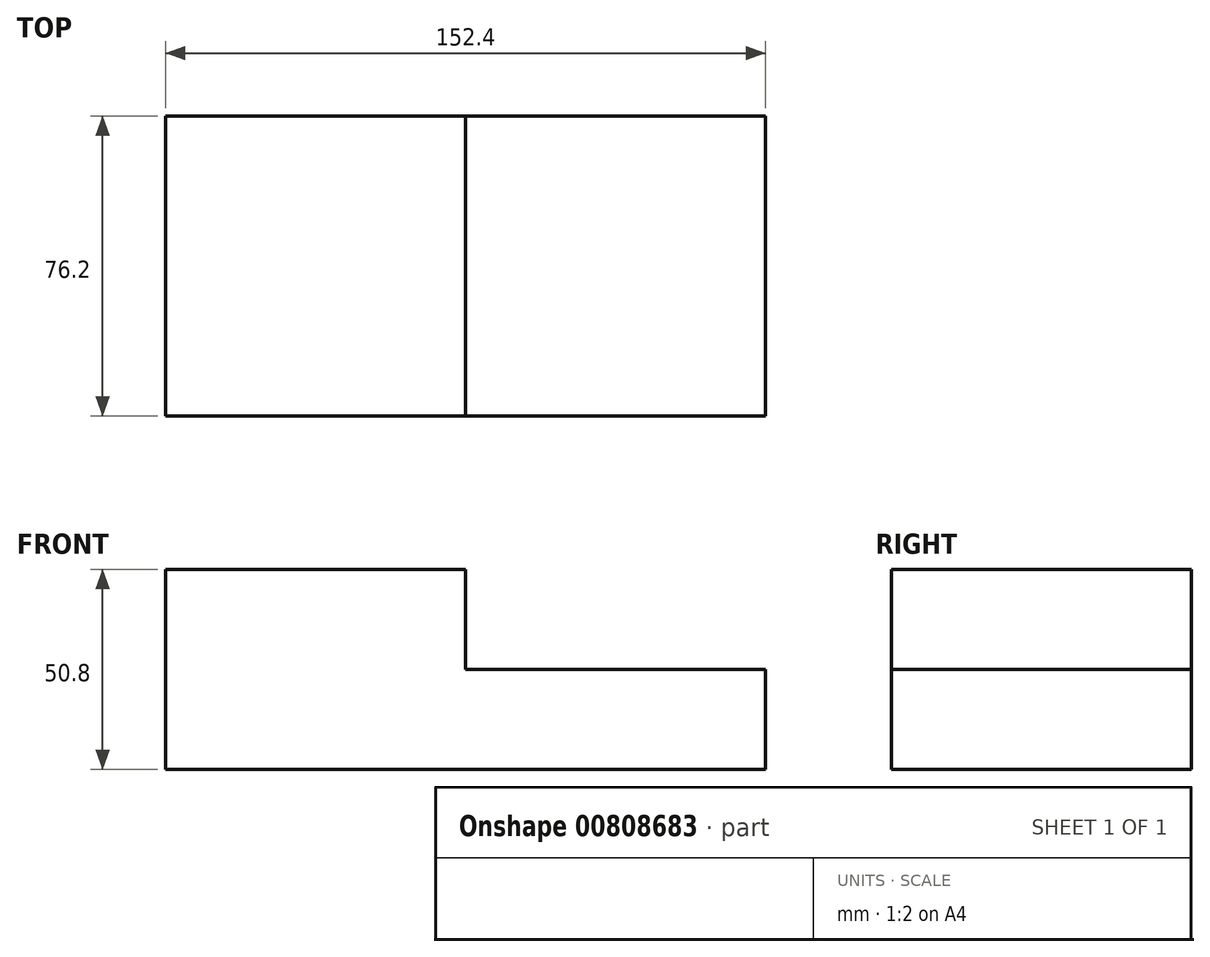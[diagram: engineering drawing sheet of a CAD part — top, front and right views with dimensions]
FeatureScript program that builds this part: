
annotation { "Feature Type Name" : "Feature", "Feature Type Description" : "" }
export const myFeature = defineFeature(function(context is Context, id is Id, definition is map)
    precondition{}
    {
        {
            var Q0;
            Q0=qCreatedBy(makeId("Front.planeOp"),FACE);
            var sketch = newSketch(context, id + "F0", { "sketchPlane" : qUnion([Q0])});
            skLineSegment(sketch, "E0", {"start": v(0, 0) * mm, "end": v(0, 50.8) * mm});
            skLineSegment(sketch, "E1", {"start": v(0, 0) * mm, "end": v(152.4, 0) * mm});
            skLineSegment(sketch, "E2", {"start": v(0, 50.8) * mm, "end": v(76.2, 50.8) * mm});
            skLineSegment(sketch, "E3", {"start": v(76.2, 50.8) * mm, "end": v(76.2, 25.4) * mm});
            skLineSegment(sketch, "E4", {"start": v(76.2, 25.4) * mm, "end": v(152.4, 25.4) * mm});
            skLineSegment(sketch, "E5", {"start": v(152.4, 25.4) * mm, "end": v(152.4, 0) * mm});
            skSolve(sketch);
        }
        {
            var Q0;
            Q0=makeQuery(id+"F0.imprint","IMPRINT",FACE,{"disambiguationData":[TD([[makeQuery(id+"F0.imprint","IMPRINT",EDGE,{"derivedFrom":sQuery(id+"F0.wireOp",EDGE,"E0")}),-1.0]])]});
            extrude(context, id + "F1", {"entities" : qUnion([Q0]), "depth" : 76.2 * mm, "offsetDistance" : 25.4 * mm});
        }
    });
